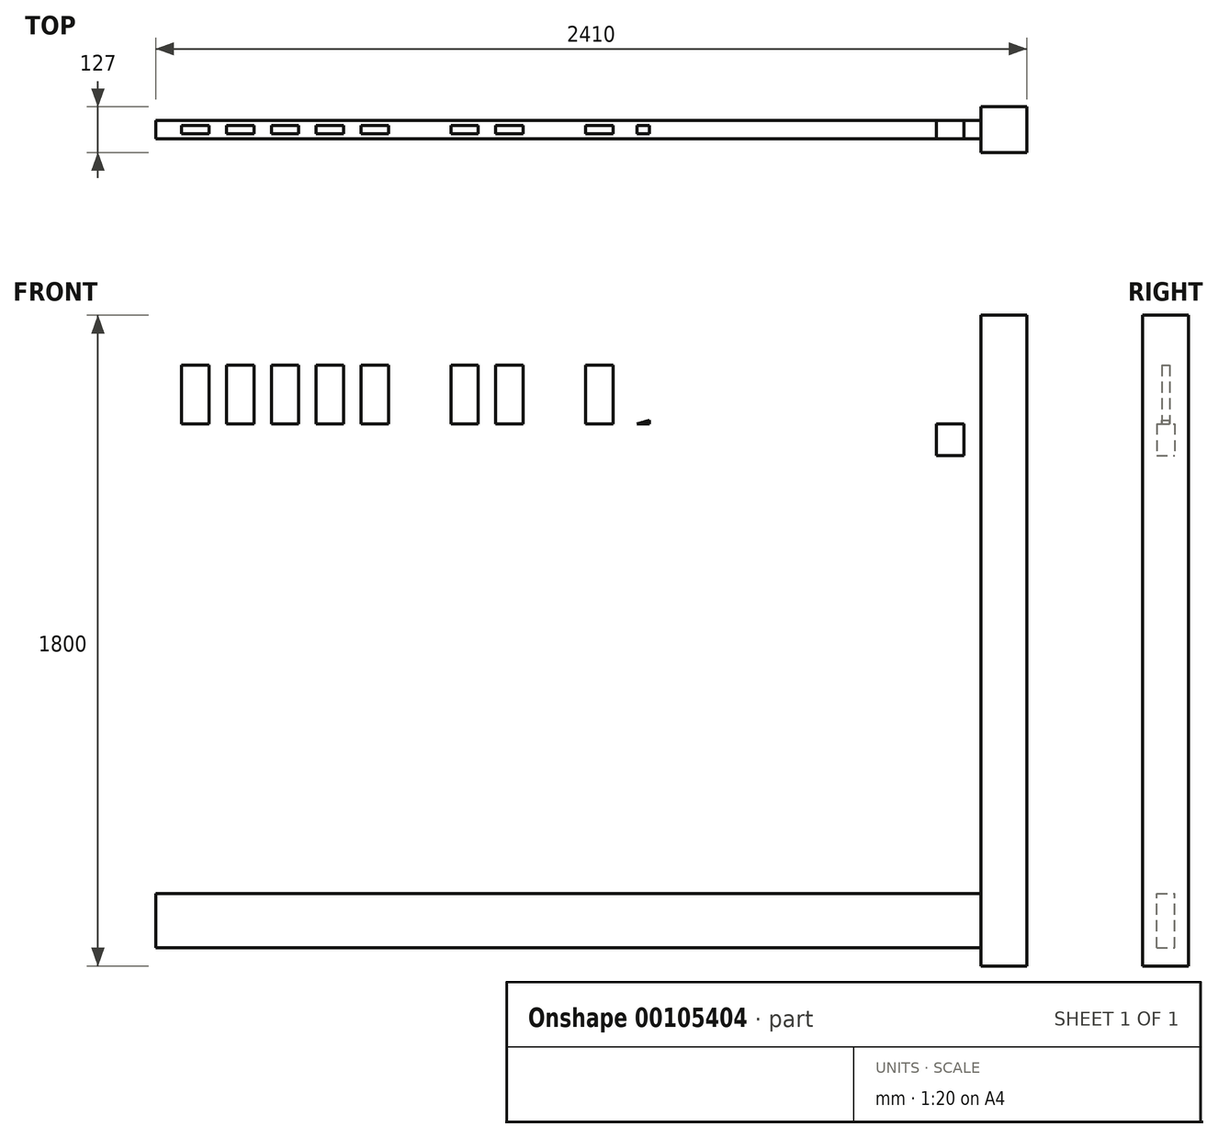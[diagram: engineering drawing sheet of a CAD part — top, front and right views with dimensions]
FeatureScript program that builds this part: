
annotation { "Feature Type Name" : "Feature", "Feature Type Description" : "" }
export const myFeature = defineFeature(function(context is Context, id is Id, definition is map)
    precondition{}
    {
        {
            var Q0;
            Q0=qCreatedBy(makeId("Front.planeOp"),FACE);
            var sketch = newSketch(context, id + "F0", { "sketchPlane" : qUnion([Q0])});
            skLineSegment(sketch, "E0.bottom", {"start": v(-499.5, 1453.98) * mm, "end": v(-372.5, 1453.98) * mm});
            skLineSegment(sketch, "E1.bottom", {"start": v(1887.27, 1437.17) * mm, "end": v(2014.27, 1437.17) * mm});
            skLineSegment(sketch, "E1.top", {"start": v(1887.27, -362.83) * mm, "end": v(2014.27, -362.83) * mm});
            skLineSegment(sketch, "E1.left", {"start": v(1887.27, 1437.17) * mm, "end": v(1887.27, -362.83) * mm});
            skLineSegment(sketch, "E1.right", {"start": v(2014.27, 1437.17) * mm, "end": v(2014.27, -362.83) * mm});
            skLineSegment(sketch, "E2", {"start": v(-372.5, 1387.17) * mm, "end": v(1887.27, 1387.17) * mm});
            skLineSegment(sketch, "E3", {"start": v(-372.5, 1299.17) * mm, "end": v(1887.27, 1299.17) * mm});
            skLineSegment(sketch, "E4", {"start": v(-372.5, 1137.17) * mm, "end": v(1887.27, 1137.17) * mm});
            skLineSegment(sketch, "E5", {"start": v(-395.82, 1049.17) * mm, "end": v(1887.27, 1049.17) * mm});
            skLineSegment(sketch, "E6", {"start": v(-395.73, -312.83) * mm, "end": v(1887.27, -312.83) * mm});
            skLineSegment(sketch, "E7", {"start": v(-395.82, -162.83) * mm, "end": v(1887.27, -162.83) * mm});
            skLineSegment(sketch, "E8", {"start": v(-324.34, 1299.17) * mm, "end": v(-324.34, 1137.17) * mm});
            skLineSegment(sketch, "E9", {"start": v(-248.34, 1299.17) * mm, "end": v(-248.34, 1137.17) * mm});
            skLineSegment(sketch, "E10", {"start": v(-200.2, 1299.17) * mm, "end": v(-200.2, 1137.17) * mm});
            skLineSegment(sketch, "E11", {"start": v(-124.2, 1299.17) * mm, "end": v(-124.2, 1137.17) * mm});
            skLineSegment(sketch, "E12", {"start": v(-76.04, 1299.17) * mm, "end": v(-76.04, 1137.17) * mm});
            skLineSegment(sketch, "E13", {"start": v(-0.04, 1299.17) * mm, "end": v(-0.04, 1137.17) * mm});
            skLineSegment(sketch, "E14", {"start": v(48.1, 1299.17) * mm, "end": v(48.1, 1137.17) * mm});
            skLineSegment(sketch, "E15", {"start": v(124.1, 1299.17) * mm, "end": v(124.1, 1137.17) * mm});
            skLineSegment(sketch, "E16", {"start": v(172.26, 1299.17) * mm, "end": v(172.26, 1137.17) * mm});
            skLineSegment(sketch, "E17", {"start": v(248.26, 1299.17) * mm, "end": v(248.26, 1137.17) * mm});
            skLineSegment(sketch, "E18", {"start": v(296.42, 1299.17) * mm, "end": v(296.42, 1137.5) * mm});
            skLineSegment(sketch, "E19", {"start": v(372.42, 1299.17) * mm, "end": v(372.42, 1137.17) * mm});
            skLineSegment(sketch, "E20", {"start": v(420.58, 1299.17) * mm, "end": v(420.58, 1137.17) * mm});
            skLineSegment(sketch, "E21", {"start": v(496.58, 1299.17) * mm, "end": v(496.58, 1137.17) * mm});
            skLineSegment(sketch, "E22", {"start": v(544.74, 1299.17) * mm, "end": v(544.74, 1137.17) * mm});
            skLineSegment(sketch, "E23", {"start": v(544.74, 1137.17) * mm, "end": v(620.74, 1137.17) * mm});
            skLineSegment(sketch, "E24", {"start": v(620.74, 1137.17) * mm, "end": v(620.74, 1299.17) * mm});
            skLineSegment(sketch, "E25", {"start": v(620.74, 1299.17) * mm, "end": v(544.74, 1299.17) * mm});
            skLineSegment(sketch, "E26.bottom", {"start": v(668.9, 1299.17) * mm, "end": v(744.9, 1299.17) * mm});
            skLineSegment(sketch, "E26.top", {"start": v(668.9, 1137.17) * mm, "end": v(744.9, 1137.17) * mm});
            skLineSegment(sketch, "E26.left", {"start": v(668.9, 1299.17) * mm, "end": v(668.9, 1137.17) * mm});
            skLineSegment(sketch, "E26.right", {"start": v(744.9, 1299.17) * mm, "end": v(744.9, 1137.17) * mm});
            skLineSegment(sketch, "E27.bottom", {"start": v(757.39, 1299.17) * mm, "end": v(969.99, 1299.17) * mm});
            skLineSegment(sketch, "E27.top", {"start": v(769, 1137.17) * mm, "end": v(969.99, 1137.17) * mm});
            skLineSegment(sketch, "E27.right", {"start": v(969.99, 1299.17) * mm, "end": v(969.99, 1137.17) * mm});
            skLineSegment(sketch, "E28.bottom", {"start": v(1094.15, 1299.17) * mm, "end": v(1094.15, 1299.17) * mm});
            skLineSegment(sketch, "E28.top", {"start": v(1094.15, 1137.17) * mm, "end": v(1094.15, 1137.17) * mm});
            skLineSegment(sketch, "E28.left", {"start": v(1094.15, 1299.17) * mm, "end": v(1094.15, 1137.17) * mm});
            skLineSegment(sketch, "E28.right", {"start": v(1094.15, 1299.17) * mm, "end": v(1094.15, 1137.17) * mm});
            skLineSegment(sketch, "E29.bottom", {"start": v(1142.3, 1299.17) * mm, "end": v(1218.3, 1299.17) * mm});
            skLineSegment(sketch, "E29.top", {"start": v(1142.3, 1137.17) * mm, "end": v(1218.3, 1137.17) * mm});
            skLineSegment(sketch, "E29.left", {"start": v(1142.3, 1299.17) * mm, "end": v(1142.3, 1137.17) * mm});
            skLineSegment(sketch, "E29.right", {"start": v(1218.3, 1299.17) * mm, "end": v(1218.3, 1137.17) * mm});
            skLineSegment(sketch, "E30.bottom", {"start": v(1266.47, 1299.17) * mm, "end": v(1342.47, 1299.17) * mm});
            skLineSegment(sketch, "E30.top", {"start": v(1266.47, 1137.17) * mm, "end": v(1342.47, 1137.17) * mm});
            skLineSegment(sketch, "E30.left", {"start": v(1266.47, 1299.17) * mm, "end": v(1266.47, 1137.17) * mm});
            skLineSegment(sketch, "E30.right", {"start": v(1342.47, 1299.17) * mm, "end": v(1342.47, 1137.17) * mm});
            skLineSegment(sketch, "E31.bottom", {"start": v(1390.63, 1299.17) * mm, "end": v(1466.63, 1299.17) * mm});
            skLineSegment(sketch, "E31.top", {"start": v(1390.63, 999.5) * mm, "end": v(1466.63, 999.5) * mm});
            skLineSegment(sketch, "E31.left", {"start": v(1390.63, 1299.17) * mm, "end": v(1390.63, 999.5) * mm});
            skLineSegment(sketch, "E31.right", {"start": v(1466.63, 1299.17) * mm, "end": v(1466.63, 999.5) * mm});
            skLineSegment(sketch, "E32.bottom", {"start": v(1514.79, 1299.17) * mm, "end": v(1590.79, 1299.17) * mm});
            skLineSegment(sketch, "E32.top", {"start": v(1514.79, 1137.17) * mm, "end": v(1590.79, 1137.17) * mm});
            skLineSegment(sketch, "E32.left", {"start": v(1514.79, 1299.17) * mm, "end": v(1514.79, 1137.17) * mm});
            skLineSegment(sketch, "E32.right", {"start": v(1590.79, 1299.17) * mm, "end": v(1590.79, 1137.17) * mm});
            skLineSegment(sketch, "E33.bottom", {"start": v(1638.95, 1299.17) * mm, "end": v(1714.95, 1299.17) * mm});
            skLineSegment(sketch, "E33.top", {"start": v(1638.95, 1137.17) * mm, "end": v(1714.95, 1137.17) * mm});
            skLineSegment(sketch, "E33.left", {"start": v(1638.95, 1299.17) * mm, "end": v(1638.95, 1137.17) * mm});
            skLineSegment(sketch, "E33.right", {"start": v(1714.95, 1299.17) * mm, "end": v(1714.95, 1137.17) * mm});
            skLineSegment(sketch, "E34.bottom", {"start": v(1763.1, 1299.17) * mm, "end": v(1839.1, 1299.17) * mm});
            skLineSegment(sketch, "E34.top", {"start": v(1763.1, 999.5) * mm, "end": v(1839.1, 999.5) * mm});
            skLineSegment(sketch, "E34.left", {"start": v(1763.1, 1299.17) * mm, "end": v(1763.1, 999.5) * mm});
            skLineSegment(sketch, "E34.right", {"start": v(1839.1, 1299.17) * mm, "end": v(1839.1, 999.5) * mm});
            skLineSegment(sketch, "E35.bottom", {"start": v(1762.29, 1315.98) * mm, "end": v(1838.29, 1315.98) * mm});
            skLineSegment(sketch, "E35.top", {"start": v(1762.29, 1137.17) * mm, "end": v(1838.29, 1137.17) * mm});
            skLineSegment(sketch, "E36", {"start": v(1018.15, 1299.17) * mm, "end": v(1018.15, 1137.17) * mm});
            skLineSegment(sketch, "E37", {"start": v(893.99, 1299.17) * mm, "end": v(893.99, 1137.17) * mm});
            skLineSegment(sketch, "E38", {"start": v(793.06, 1299.17) * mm, "end": v(793.06, 1137.17) * mm});
            skLineSegment(sketch, "E39", {"start": v(869.06, 1299.17) * mm, "end": v(869.06, 1137.17) * mm});
            skLineSegment(sketch, "E40.bottom", {"start": v(-395.73, -362.83) * mm, "end": v(-522.73, -362.83) * mm});
            skLineSegment(sketch, "E40.top", {"start": v(-395.73, 837.17) * mm, "end": v(-522.73, 837.17) * mm});
            skLineSegment(sketch, "E40.left", {"start": v(-395.73, -362.83) * mm, "end": v(-395.73, 837.17) * mm});
            skLineSegment(sketch, "E40.right", {"start": v(-522.73, -362.83) * mm, "end": v(-522.73, 837.17) * mm});
            skLineSegment(sketch, "E41", {"start": v(-395.73, 787.17) * mm, "end": v(1887.27, 1387.17) * mm});
            skLineSegment(sketch, "E42", {"start": v(1887.27, 1296.18) * mm, "end": v(-395.73, 696.18) * mm});
            skLineSegment(sketch, "E43", {"start": v(1888.49, 986.31) * mm, "end": v(-413.97, 381.2) * mm});
            skLineSegment(sketch, "E44", {"start": v(-325.68, 404.4) * mm, "end": v(-325.68, 714.6) * mm});
            skLineSegment(sketch, "E45", {"start": v(-249.68, 424.38) * mm, "end": v(-249.68, 734.56) * mm});
            skLineSegment(sketch, "E46", {"start": v(-413.97, 381.2) * mm, "end": v(-395.73, 311.8) * mm});
            skLineSegment(sketch, "E47", {"start": v(-418.1, 665.5) * mm, "end": v(-395.73, 580.39) * mm});
            skLineSegment(sketch, "E48", {"start": v(1784.09, -162.83) * mm, "end": v(1784.09, 1049.17) * mm});
            skSolve(sketch);
        }
        {
            var Q0;
            {var subQ1=sQuery(id+"F0.wireOp",EDGE,"E0.bottom");Q0=makeQuery(id+"F0.imprint","IMPRINT",FACE,{"disambiguationData":[TD([[makeQuery(id+"F0.imprint","IMPRINT",EDGE,{"derivedFrom":subQ1}),-1.0]])]});}
            var Q1;
            {var subQ5=sQuery(id+"F0.wireOp",EDGE,"E1.bottom");Q1=makeQuery(id+"F0.imprint","IMPRINT",FACE,{"disambiguationData":[TD([[makeQuery(id+"F0.imprint","IMPRINT",EDGE,{"derivedFrom":subQ5}),-1.0]])]});}
            extrude(context, id + "F1", {"entities" : qUnion([Q0, Q1]), "depth" : 63.5 * mm, "hasSecondDirection" : true, "secondDirectionOppositeDirection" : true, "secondDirectionDepth" : 63.5 * mm});
        }
        {
            var Q0;
            {var subQ23=sQuery(id+"F0.wireOp",EDGE,"E2");Q0=makeQuery(id+"F0.imprint","IMPRINT",FACE,{"disambiguationData":[TD([[makeQuery(id+"F0.imprint","IMPRINT",EDGE,{"derivedFrom":subQ23}),-1.0]])]});}
            var Q1;
            {var subQ31=sQuery(id+"F0.wireOp",EDGE,"E5");Q1=makeQuery(id+"F0.imprint","IMPRINT",FACE,{"disambiguationData":[TD([[makeQuery(id+"F0.imprint","IMPRINT",EDGE,{"derivedFrom":subQ31}),1.0]])]});}
            var Q2;
            {var subQ0=sQuery(id+"F0.wireOp",EDGE,"E6");Q2=makeQuery(id+"F0.imprint","IMPRINT",FACE,{"disambiguationData":[TD([[makeQuery(id+"F0.imprint","IMPRINT",EDGE,{"derivedFrom":subQ0}),1.0]])]});}
            extrude(context, id + "F2", {"entities" : qUnion([Q0, Q1, Q2]), "depth" : 25 * mm, "hasSecondDirection" : true, "secondDirectionOppositeDirection" : true, "secondDirectionDepth" : 25 * mm});
        }
        {
            var Q0;
            {var subQ0=sQuery(id+"F0.wireOp",EDGE,"E8");Q0=makeQuery(id+"F0.imprint","IMPRINT",FACE,{"disambiguationData":[TD([[makeQuery(id+"F0.imprint","IMPRINT",EDGE,{"derivedFrom":subQ0}),1.0]])]});}
            var Q1;
            {var subQ0=sQuery(id+"F0.wireOp",EDGE,"E10");Q1=makeQuery(id+"F0.imprint","IMPRINT",FACE,{"disambiguationData":[TD([[makeQuery(id+"F0.imprint","IMPRINT",EDGE,{"derivedFrom":subQ0}),1.0]])]});}
            var Q2;
            {var subQ0=sQuery(id+"F0.wireOp",EDGE,"E12");Q2=makeQuery(id+"F0.imprint","IMPRINT",FACE,{"disambiguationData":[TD([[makeQuery(id+"F0.imprint","IMPRINT",EDGE,{"derivedFrom":subQ0}),1.0]])]});}
            var Q3;
            {var subQ0=sQuery(id+"F0.wireOp",EDGE,"E14");Q3=makeQuery(id+"F0.imprint","IMPRINT",FACE,{"disambiguationData":[TD([[makeQuery(id+"F0.imprint","IMPRINT",EDGE,{"derivedFrom":subQ0}),1.0]])]});}
            var Q4;
            {var subQ0=sQuery(id+"F0.wireOp",EDGE,"E16");Q4=makeQuery(id+"F0.imprint","IMPRINT",FACE,{"disambiguationData":[TD([[makeQuery(id+"F0.imprint","IMPRINT",EDGE,{"derivedFrom":subQ0}),1.0]])]});}
            var Q5;
            {var subQ0=sQuery(id+"F0.wireOp",EDGE,"E18");Q5=makeQuery(id+"F0.imprint","IMPRINT",FACE,{"disambiguationData":[TD([[makeQuery(id+"F0.imprint","IMPRINT",EDGE,{"derivedFrom":subQ0}),1.0]])]});}
            var Q6;
            {var subQ0=sQuery(id+"F0.wireOp",EDGE,"E20");Q6=makeQuery(id+"F0.imprint","IMPRINT",FACE,{"disambiguationData":[TD([[makeQuery(id+"F0.imprint","IMPRINT",EDGE,{"derivedFrom":subQ0}),1.0]])]});}
            var Q7;
            Q7=makeQuery(id+"F0.imprint","IMPRINT",FACE,{"disambiguationData":[TD([[makeQuery(id+"F0.imprint","IMPRINT",EDGE,{"derivedFrom":sQuery(id+"F0.wireOp",EDGE,"E22")}),1.0]])]});
            var Q8;
            Q8=makeQuery(id+"F0.imprint","IMPRINT",FACE,{"disambiguationData":[TD([[makeQuery(id+"F0.imprint","IMPRINT",EDGE,{"derivedFrom":sQuery(id+"F0.wireOp",EDGE,"E26.bottom")}),-1.0]])]});
            var Q9;
            {var subQ0=sQuery(id+"F0.wireOp",EDGE,"E38");Q9=makeQuery(id+"F0.imprint","IMPRINT",FACE,{"disambiguationData":[TD([[makeQuery(id+"F0.imprint","IMPRINT",EDGE,{"derivedFrom":subQ0}),1.0]])]});}
            var Q10;
            {var subQ0=sQuery(id+"F0.wireOp",EDGE,"E27.right");Q10=makeQuery(id+"F0.imprint","IMPRINT",FACE,{"disambiguationData":[TD([[makeQuery(id+"F0.imprint","IMPRINT",EDGE,{"derivedFrom":subQ0}),-1.0]])]});}
            var Q11;
            {var subQ0=sQuery(id+"F0.wireOp",EDGE,"E28.right");Q11=makeQuery(id+"F0.imprint","IMPRINT",FACE,{"disambiguationData":[TD([[makeQuery(id+"F0.imprint","IMPRINT",EDGE,{"derivedFrom":subQ0}),-1.0]])]});}
            var Q12;
            Q12=makeQuery(id+"F0.imprint","IMPRINT",FACE,{"disambiguationData":[TD([[makeQuery(id+"F0.imprint","IMPRINT",EDGE,{"derivedFrom":sQuery(id+"F0.wireOp",EDGE,"E29.bottom")}),-1.0]])]});
            var Q13;
            Q13=makeQuery(id+"F0.imprint","IMPRINT",FACE,{"disambiguationData":[TD([[makeQuery(id+"F0.imprint","IMPRINT",EDGE,{"derivedFrom":sQuery(id+"F0.wireOp",EDGE,"E30.bottom")}),-1.0]])]});
            var Q14;
            Q14=makeQuery(id+"F0.imprint","IMPRINT",FACE,{"disambiguationData":[TD([[makeQuery(id+"F0.imprint","IMPRINT",EDGE,{"derivedFrom":sQuery(id+"F0.wireOp",EDGE,"E31.bottom")}),-1.0]])]});
            var Q15;
            Q15=makeQuery(id+"F0.imprint","IMPRINT",FACE,{"disambiguationData":[TD([[makeQuery(id+"F0.imprint","IMPRINT",EDGE,{"derivedFrom":sQuery(id+"F0.wireOp",EDGE,"E32.bottom")}),-1.0]])]});
            var Q16;
            Q16=makeQuery(id+"F0.imprint","IMPRINT",FACE,{"disambiguationData":[TD([[makeQuery(id+"F0.imprint","IMPRINT",EDGE,{"derivedFrom":sQuery(id+"F0.wireOp",EDGE,"E33.bottom")}),-1.0]])]});
            var Q17;
            {var subQ2=sQuery(id+"F0.wireOp",EDGE,"E34.bottom");Q17=makeQuery(id+"F0.imprint","IMPRINT",FACE,{"disambiguationData":[TD([[makeQuery(id+"F0.imprint","IMPRINT",EDGE,{"derivedFrom":subQ2}),-1.0]])]});}
            extrude(context, id + "F3", {"entities" : qUnion([Q0, Q1, Q2, Q3, Q4, Q5, Q6, Q7, Q8, Q9, Q10, Q11, Q12, Q13, Q14, Q15, Q16, Q17]), "depth" : 11 * mm, "hasSecondDirection" : true, "secondDirectionOppositeDirection" : true, "secondDirectionDepth" : 11 * mm});
        }
    });
